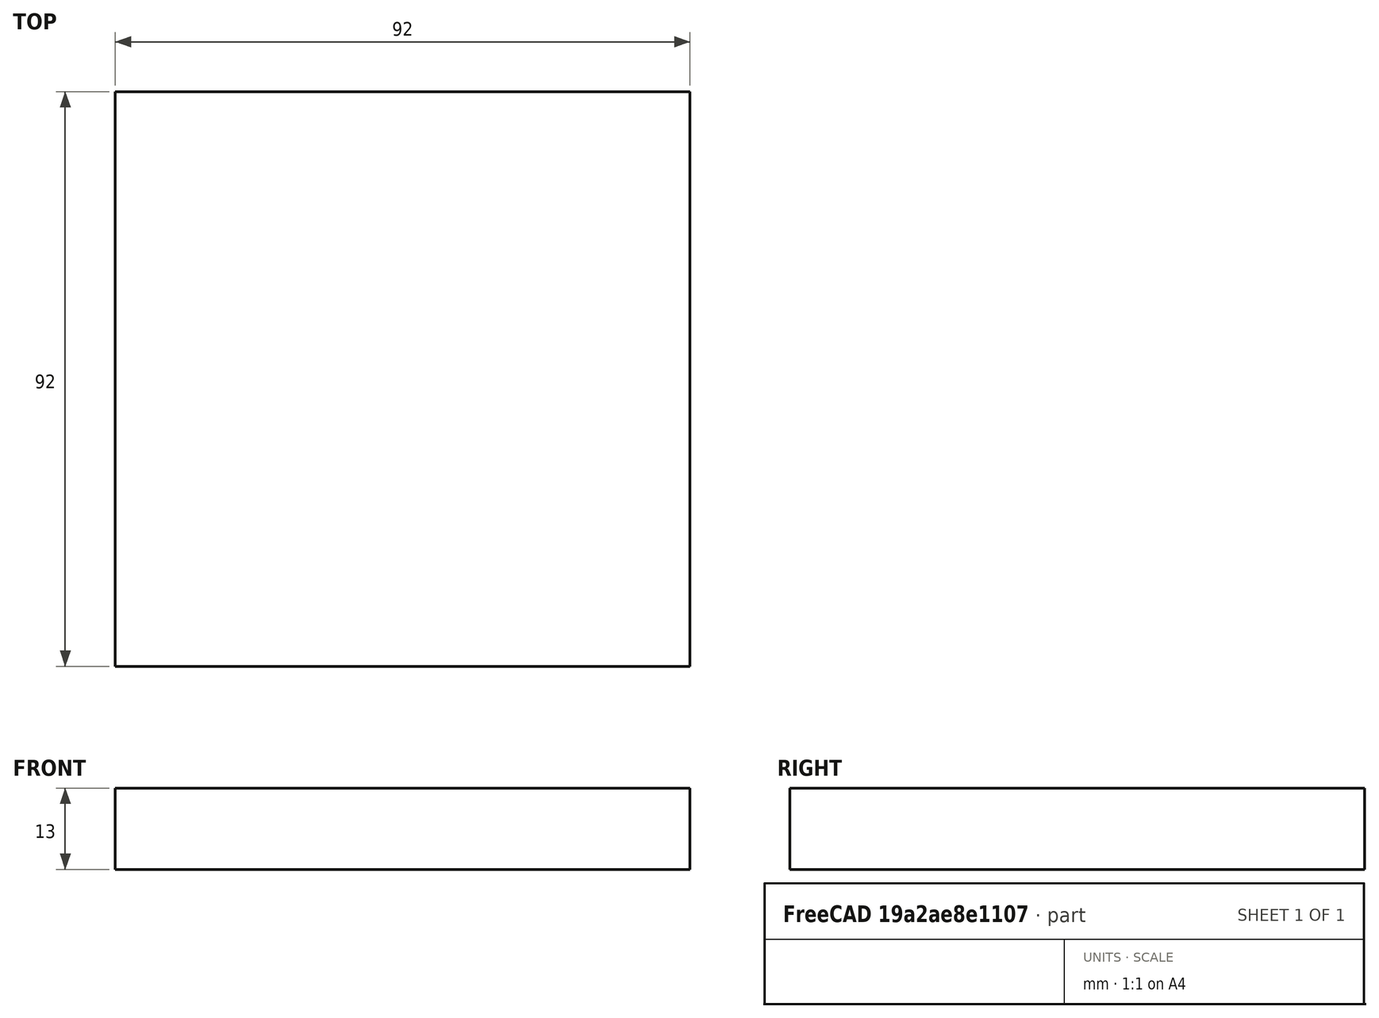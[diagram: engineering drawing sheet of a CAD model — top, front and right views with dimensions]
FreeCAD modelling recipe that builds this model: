
FCSTD DOCUMENT  (FreeCAD 0.19R24276 (Git))
Label: fan-filter
License: All rights reserved
LicenseURL: http://en.wikipedia.org/wiki/All_rights_reserved
objects: Sketcher::SketchObject×1, PartDesign::Pad×1, PartDesign::Body×1
note: 4 computed .brp shape members not serialized (recipe doc carries the construction recipe); baked Part::Feature solids carry a one-line shape summary decoded from their .brp

FEATURE [Sketcher::SketchObject] Sketch
  FullyConstrained = true
  MapMode = 5
  Support = -> [XY_Plane]
  sketch-geometry (4):
    g0: LineSegment StartX=-46 StartY=46 StartZ=0 EndX=46 EndY=46 EndZ=0
    g1: LineSegment StartX=46 StartY=46 StartZ=0 EndX=46 EndY=-46 EndZ=0
    g2: LineSegment StartX=46 StartY=-46 StartZ=0 EndX=-46 EndY=-46 EndZ=0
    g3: LineSegment StartX=-46 StartY=-46 StartZ=0 EndX=-46 EndY=46 EndZ=0
  constraints (12):
    c: Coincident(g0,g1)
    c: Coincident(g1,g2)
    c: Coincident(g2,g3)
    c: Coincident(g3,g0)
    c: Horizontal(g0)
    c: Horizontal(g2)
    c: Vertical(g1)
    c: Vertical(g3)
    c: DistanceX(g0,g-1) = 46
    c: DistanceX(g-1,g0) = 46
    c: DistanceY(g-1,g0) = 46
    c: DistanceY(g2,g-1) = 46
FEATURE [PartDesign::Pad] Pad
  Direction = (1,1,1)
  Length = 13
  Length2 = 100
  Profile = -> Sketch
  Type = 0
FEATURE [PartDesign::Body] Body
  Group = -> [Sketch,Pad]
  Origin = -> Origin
  Tip = -> Pad
